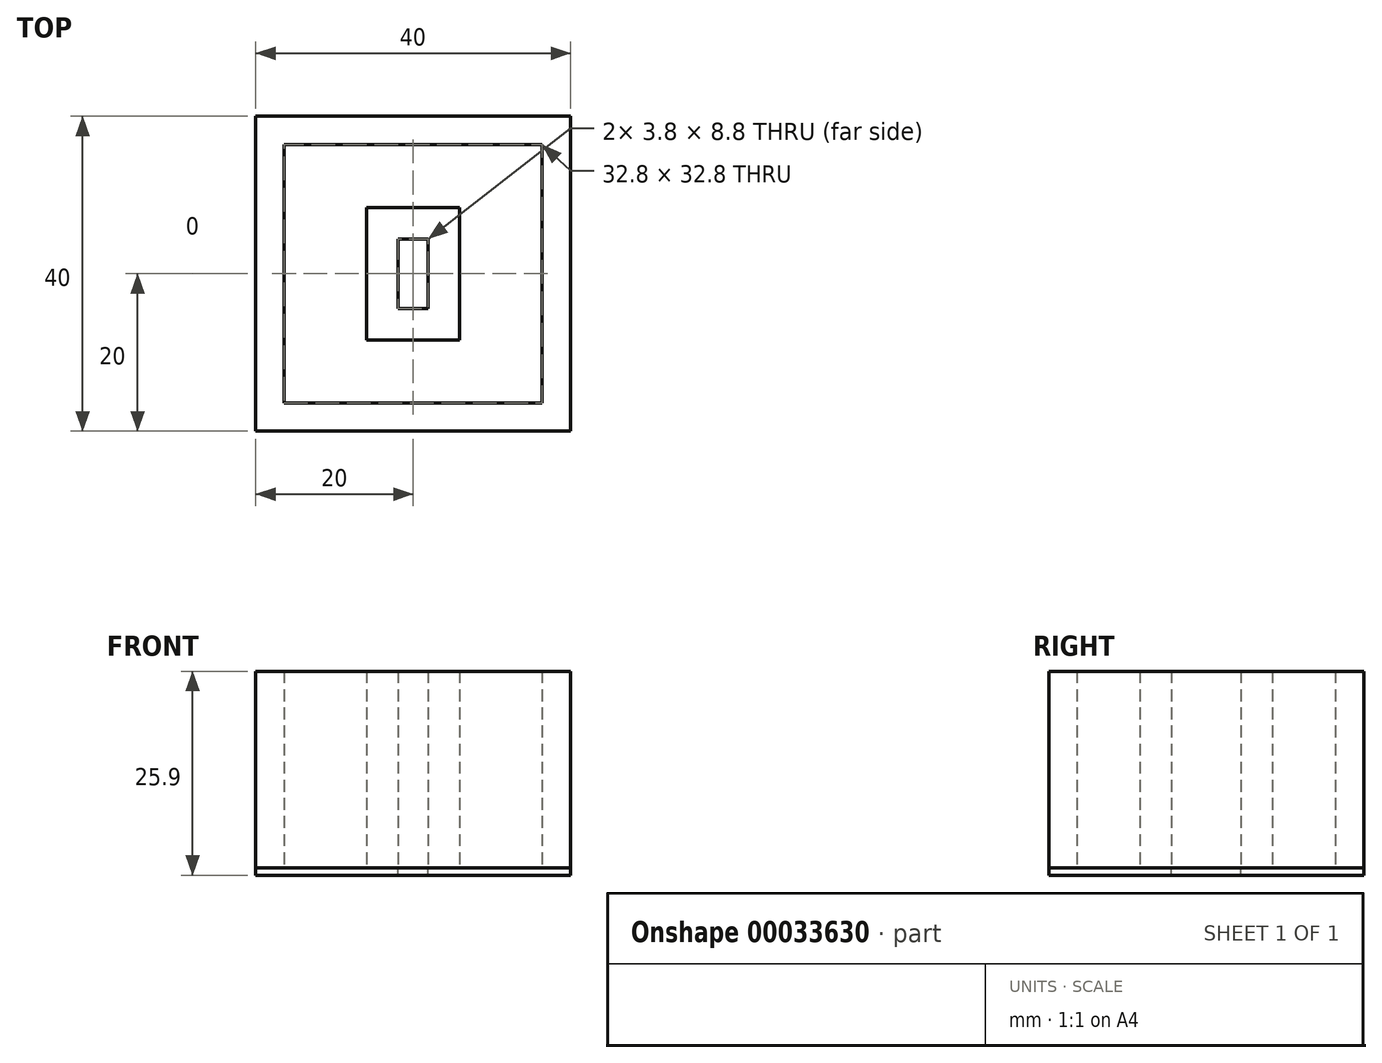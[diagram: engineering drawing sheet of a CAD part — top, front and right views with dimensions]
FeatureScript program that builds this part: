
annotation { "Feature Type Name" : "Feature", "Feature Type Description" : "" }
export const myFeature = defineFeature(function(context is Context, id is Id, definition is map)
    precondition{}
    {
        {
            var Q0;
            Q0=qCreatedBy(makeId("Top.planeOp"),FACE);
            var sketch = newSketch(context, id + "F0", { "sketchPlane" : qUnion([Q0])});
            skLineSegment(sketch, "E0.bottom", {"start": v(-20, 20) * mm, "end": v(20, 20) * mm});
            skLineSegment(sketch, "E0.top", {"start": v(-20, -20) * mm, "end": v(20, -20) * mm});
            skLineSegment(sketch, "E0.left", {"start": v(-20, 20) * mm, "end": v(-20, -20) * mm});
            skLineSegment(sketch, "E0.right", {"start": v(20, 20) * mm, "end": v(20, -20) * mm});
            skLineSegment(sketch, "E1.0", {"start": v(-16.4, 16.4) * mm, "end": v(-16.4, -16.4) * mm});
            skLineSegment(sketch, "E2.0", {"start": v(-16.4, -16.4) * mm, "end": v(16.4, -16.4) * mm});
            skLineSegment(sketch, "E2.1", {"start": v(16.4, 16.4) * mm, "end": v(16.4, -16.4) * mm});
            skLineSegment(sketch, "E2.2", {"start": v(-16.4, 16.4) * mm, "end": v(16.4, 16.4) * mm});
            skSolve(sketch);
        }
        {
            var Q0;
            Q0 = qSketchRegion(id + "F0", true);
            extrude(context, id + "F1", {"entities" : qUnion([Q0]), "depth" : 25 * mm});
        }
        {
            var Q0;
            Q0=qCreatedBy(makeId("Top.planeOp"),FACE);
            var sketch = newSketch(context, id + "F2", { "sketchPlane" : qUnion([Q0])});
            skLineSegment(sketch, "E3.bottom", {"start": v(-1.9, 4.4) * mm, "end": v(1.9, 4.4) * mm});
            skLineSegment(sketch, "E3.right", {"start": v(1.9, 4.4) * mm, "end": v(1.9, -4.4) * mm});
            skLineSegment(sketch, "E3.top", {"start": v(-1.9, -4.4) * mm, "end": v(1.9, -4.4) * mm});
            skLineSegment(sketch, "E3.left", {"start": v(-1.9, 4.4) * mm, "end": v(-1.9, -4.4) * mm});
            skLineSegment(sketch, "E4.0", {"start": v(-5.9, 8.4) * mm, "end": v(5.9, 8.4) * mm});
            skLineSegment(sketch, "E4.1", {"start": v(-5.9, 8.4) * mm, "end": v(-5.9, -8.4) * mm});
            skLineSegment(sketch, "E4.2", {"start": v(-5.9, -8.4) * mm, "end": v(5.9, -8.4) * mm});
            skLineSegment(sketch, "E4.3", {"start": v(5.9, 8.4) * mm, "end": v(5.9, -8.4) * mm});
            skSolve(sketch);
        }
        {
            var Q0;
            Q0 = qSketchRegion(id + "F2", true);
            extrude(context, id + "F3", {"entities" : qUnion([Q0]), "depth" : 25 * mm});
        }
        {
            var Q0;
            Q0=makeQuery(id+"F1.opExtrude","CAP_FACE",FACE,{"disambiguationData":[OSD([sQuery(id+"F0.wireOp",EDGE,"E0.bottom"),sQuery(id+"F0.wireOp",EDGE,"E0.top"),sQuery(id+"F0.wireOp",EDGE,"E0.left"),sQuery(id+"F0.wireOp",EDGE,"E0.right"),sQuery(id+"F0.wireOp",EDGE,"E1.0"),sQuery(id+"F0.wireOp",EDGE,"E2.0"),sQuery(id+"F0.wireOp",EDGE,"E2.1"),sQuery(id+"F0.wireOp",EDGE,"E2.2")])],"isStart":true});
            var sketch = newSketch(context, id + "F4", { "sketchPlane" : qUnion([Q0])});
            skLineSegment(sketch, "E5.0", {"start": v(20, -20) * mm, "end": v(20, 20) * mm});
            skLineSegment(sketch, "E6.0", {"start": v(-20, 20) * mm, "end": v(20, 20) * mm});
            skLineSegment(sketch, "E7.0", {"start": v(-20, -20) * mm, "end": v(20, -20) * mm});
            skLineSegment(sketch, "E8.0", {"start": v(-20, -20) * mm, "end": v(-20, 20) * mm});
            skLineSegment(sketch, "E9.0", {"start": v(1.9, -4.4) * mm, "end": v(1.9, 4.4) * mm});
            skLineSegment(sketch, "E10.0", {"start": v(-1.9, 4.4) * mm, "end": v(1.9, 4.4) * mm});
            skLineSegment(sketch, "E11.0", {"start": v(-1.9, -4.4) * mm, "end": v(-1.9, 4.4) * mm});
            skLineSegment(sketch, "E12.0", {"start": v(-1.9, -4.4) * mm, "end": v(1.9, -4.4) * mm});
            skSolve(sketch);
        }
        {
            var Q0;
            Q0 = qSketchRegion(id + "F4", true);
            extrude(context, id + "F5", {"entities" : qUnion([Q0]), "depth" : .9 * mm});
        }
    });
